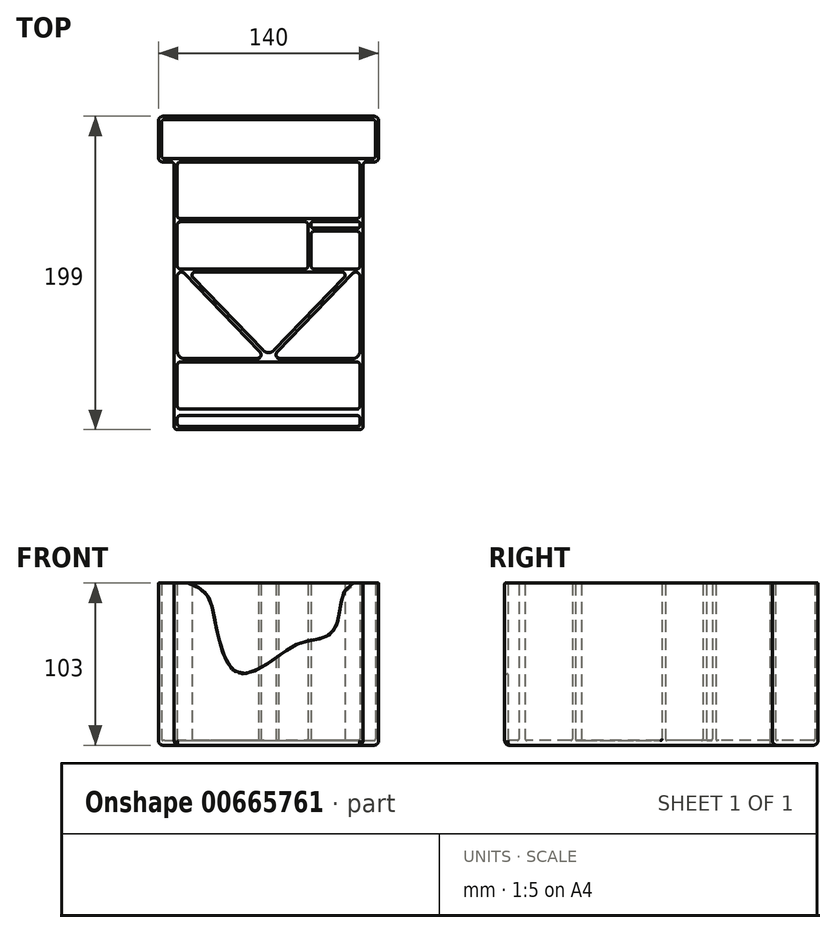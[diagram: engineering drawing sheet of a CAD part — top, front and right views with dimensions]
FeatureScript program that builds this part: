
annotation { "Feature Type Name" : "Feature", "Feature Type Description" : "" }
export const myFeature = defineFeature(function(context is Context, id is Id, definition is map)
    precondition{}
    {
        {
            var Q0;
            Q0=qCreatedBy(makeId("Top.planeOp"),FACE);
            var sketch = newSketch(context, id + "F0", { "sketchPlane" : qUnion([Q0])});
            skLineSegment(sketch, "E0.bottom", {"start": v(-61.93, 44.26) * mm, "end": v(-67, 44.26) * mm});
            skLineSegment(sketch, "E0.top", {"start": v(67, 73.26) * mm, "end": v(-67, 73.26) * mm});
            skLineSegment(sketch, "E0.left", {"start": v(70, 47.26) * mm, "end": v(70, 70.26) * mm});
            skLineSegment(sketch, "E0.right", {"start": v(-70, 47.26) * mm, "end": v(-70, 70.26) * mm});
            skPoint(sketch, "E0.middle", {"position": v(0, 58.76) * mm});
            skLineSegment(sketch, "E1", {"start": v(-70, 0) * mm, "end": v(70.86, 0) * mm, "construction": true});
            skLineSegment(sketch, "E2", {"start": v(-59.96, 42.57) * mm, "end": v(-59.96, -123.74) * mm});
            skLineSegment(sketch, "E3", {"start": v(60.04, 42.26) * mm, "end": v(60.04, -123.66) * mm});
            skLineSegment(sketch, "E4", {"start": v(57.04, 2.26) * mm, "end": v(28.04, 2.26) * mm});
            skLineSegment(sketch, "E5", {"start": v(-57.96, -125.74) * mm, "end": v(57.96, -125.74) * mm});
            skLineSegment(sketch, "E6.bottom", {"start": v(-55.96, 6.26) * mm, "end": v(23.04, 6.26) * mm});
            skLineSegment(sketch, "E6.top", {"start": v(-55.96, -23.74) * mm, "end": v(23.04, -23.74) * mm});
            skLineSegment(sketch, "E6.left", {"start": v(-57.96, 4.26) * mm, "end": v(-57.96, -21.74) * mm});
            skLineSegment(sketch, "E6.right", {"start": v(25.04, 4.26) * mm, "end": v(25.04, -21.74) * mm});
            skLineSegment(sketch, "E7.bottom", {"start": v(29.04, 0.26) * mm, "end": v(56.04, 0.26) * mm});
            skLineSegment(sketch, "E7.top", {"start": v(29.04, -23.74) * mm, "end": v(56.04, -23.74) * mm});
            skLineSegment(sketch, "E7.left", {"start": v(27.04, -1.74) * mm, "end": v(27.04, -21.74) * mm});
            skLineSegment(sketch, "E7.right", {"start": v(58.04, -1.74) * mm, "end": v(58.04, -21.74) * mm});
            skLineSegment(sketch, "E8", {"start": v(58.04, 3.26) * mm, "end": v(58.04, 5.26) * mm});
            skLineSegment(sketch, "E9", {"start": v(-46.62, -25.74) * mm, "end": v(46.62, -25.74) * mm});
            skLineSegment(sketch, "E10", {"start": v(-3.6, -75.32) * mm, "end": v(-48.06, -29.13) * mm});
            skPoint(sketch, "E11.newPointA", {"position": v(-10.52, -65.55) * mm});
            skPoint(sketch, "E12", {"position": v(0, -79.06) * mm});
            skPoint(sketch, "E13.visualSharp", {"position": v(-51.32, -25.74) * mm});
            skArc(sketch, "E13.filletArc", {"start": v(-46.62, -25.74) * mm, "mid": v(-48.46, -26.96) * mm, "end": v(-48.06, -29.13) * mm});
            skPoint(sketch, "E14.visualSharp", {"position": v(-57.96, -23.74) * mm});
            skArc(sketch, "E14.filletArc", {"start": v(-57.96, -21.74) * mm, "mid": v(-57.37, -23.16) * mm, "end": v(-55.96, -23.74) * mm});
            skPoint(sketch, "E15.visualSharp", {"position": v(25.04, -23.74) * mm});
            skArc(sketch, "E15.filletArc", {"start": v(23.04, -23.74) * mm, "mid": v(24.46, -23.16) * mm, "end": v(25.04, -21.74) * mm});
            skArc(sketch, "E16.filletArc", {"start": v(27.04, -21.74) * mm, "mid": v(27.63, -23.16) * mm, "end": v(29.04, -23.74) * mm});
            skPoint(sketch, "E17.visualSharp", {"position": v(25.04, 6.26) * mm});
            skArc(sketch, "E17.filletArc", {"start": v(25.04, 4.26) * mm, "mid": v(24.46, 5.67) * mm, "end": v(23.04, 6.26) * mm});
            skArc(sketch, "E18.filletArc", {"start": v(56.04, -23.74) * mm, "mid": v(57.46, -23.16) * mm, "end": v(58.04, -21.74) * mm});
            skPoint(sketch, "E19.visualSharp", {"position": v(-57.96, 6.26) * mm});
            skArc(sketch, "E19.filletArc", {"start": v(-55.96, 6.26) * mm, "mid": v(-57.37, 5.67) * mm, "end": v(-57.96, 4.26) * mm});
            skPoint(sketch, "E20.visualSharp", {"position": v(70, 44.26) * mm});
            skArc(sketch, "E20.filletArc", {"start": v(67, 44.26) * mm, "mid": v(69.12, 45.14) * mm, "end": v(70, 47.26) * mm});
            skPoint(sketch, "E21.visualSharp", {"position": v(-70, 44.26) * mm});
            skArc(sketch, "E21.filletArc", {"start": v(-70, 47.26) * mm, "mid": v(-69.12, 45.14) * mm, "end": v(-67, 44.26) * mm});
            skPoint(sketch, "E22.visualSharp", {"position": v(-70, 73.26) * mm});
            skArc(sketch, "E22.filletArc", {"start": v(-67, 73.26) * mm, "mid": v(-69.12, 72.38) * mm, "end": v(-70, 70.26) * mm});
            skPoint(sketch, "E23.visualSharp", {"position": v(70, 73.26) * mm});
            skArc(sketch, "E23.filletArc", {"start": v(70, 70.26) * mm, "mid": v(69.12, 72.38) * mm, "end": v(67, 73.26) * mm});
            skPoint(sketch, "E24.visualSharp", {"position": v(58, 1.67) * mm});
            skLineSegment(sketch, "E25", {"start": v(3.6, -75.32) * mm, "end": v(48.06, -29.13) * mm});
            skPoint(sketch, "E26.visualSharp", {"position": v(51.32, -25.74) * mm});
            skArc(sketch, "E26.filletArc", {"start": v(48.06, -29.13) * mm, "mid": v(48.46, -26.96) * mm, "end": v(46.62, -25.74) * mm});
            skArc(sketch, "E27.filletArc", {"start": v(-3.6, -75.32) * mm, "mid": v(0, -76.85) * mm, "end": v(3.6, -75.32) * mm});
            skPoint(sketch, "E28.startSnap0", {"position": v(0, -76.85) * mm});
            skArc(sketch, "E29.MirrorCS", {"start": v(53.28, -26.6) * mm, "mid": v(56.3, -25.94) * mm, "end": v(58.04, -28.51) * mm});
            skLineSegment(sketch, "E30.MirrorCS", {"start": v(58.04, -28.51) * mm, "end": v(58.04, -75.72) * mm});
            skArc(sketch, "E31.MirrorCS", {"start": v(58.04, -75.72) * mm, "mid": v(56.57, -79.28) * mm, "end": v(53, -80.76) * mm});
            skLineSegment(sketch, "E32.MirrorCS", {"start": v(5.61, -76.11) * mm, "end": v(53.28, -26.6) * mm});
            skLineSegment(sketch, "E33.MirrorCS", {"start": v(53, -80.76) * mm, "end": v(6.4, -80.76) * mm});
            skArc(sketch, "E34.MirrorCS", {"start": v(6.4, -80.76) * mm, "mid": v(4.83, -78.63) * mm, "end": v(5.61, -76.11) * mm});
            skLineSegment(sketch, "E35.bottom", {"start": v(-55.96, -82.76) * mm, "end": v(56.04, -82.76) * mm});
            skLineSegment(sketch, "E35.top", {"start": v(-55.96, -112.76) * mm, "end": v(56.04, -112.76) * mm});
            skLineSegment(sketch, "E35.left", {"start": v(-57.96, -84.76) * mm, "end": v(-57.96, -110.76) * mm});
            skLineSegment(sketch, "E35.right", {"start": v(58.04, -84.76) * mm, "end": v(58.04, -110.76) * mm});
            skPoint(sketch, "E36.visualSharp", {"position": v(-57.96, -82.76) * mm});
            skArc(sketch, "E36.filletArc", {"start": v(-55.96, -82.76) * mm, "mid": v(-57.37, -83.34) * mm, "end": v(-57.96, -84.76) * mm});
            skPoint(sketch, "E37.visualSharp", {"position": v(58.04, -82.76) * mm});
            skArc(sketch, "E37.filletArc", {"start": v(58.04, -84.76) * mm, "mid": v(57.46, -83.34) * mm, "end": v(56.04, -82.76) * mm});
            skPoint(sketch, "E38.visualSharp", {"position": v(58.04, -112.76) * mm});
            skArc(sketch, "E38.filletArc", {"start": v(56.04, -112.76) * mm, "mid": v(57.46, -112.17) * mm, "end": v(58.04, -110.76) * mm});
            skPoint(sketch, "E39.visualSharp", {"position": v(-57.96, -112.76) * mm});
            skArc(sketch, "E39.filletArc", {"start": v(-57.96, -110.76) * mm, "mid": v(-57.37, -112.17) * mm, "end": v(-55.96, -112.76) * mm});
            skLineSegment(sketch, "E40.bottom", {"start": v(-55.96, -116.74) * mm, "end": v(56.04, -116.74) * mm});
            skLineSegment(sketch, "E40.top", {"start": v(-55.96, -123.74) * mm, "end": v(56.04, -123.74) * mm});
            skLineSegment(sketch, "E40.left", {"start": v(-57.96, -118.74) * mm, "end": v(-57.96, -121.74) * mm});
            skLineSegment(sketch, "E40.right", {"start": v(58.04, -118.74) * mm, "end": v(58.04, -121.74) * mm});
            skPoint(sketch, "E41.visualSharp", {"position": v(58.04, -116.74) * mm});
            skArc(sketch, "E41.filletArc", {"start": v(58.04, -118.74) * mm, "mid": v(57.46, -117.33) * mm, "end": v(56.04, -116.74) * mm});
            skPoint(sketch, "E42.visualSharp", {"position": v(58.04, -123.74) * mm});
            skArc(sketch, "E42.filletArc", {"start": v(56.04, -123.74) * mm, "mid": v(57.46, -123.16) * mm, "end": v(58.04, -121.74) * mm});
            skPoint(sketch, "E43.visualSharp", {"position": v(-57.96, -123.74) * mm});
            skArc(sketch, "E43.filletArc", {"start": v(-57.96, -121.74) * mm, "mid": v(-57.37, -123.16) * mm, "end": v(-55.96, -123.74) * mm});
            skPoint(sketch, "E44.visualSharp", {"position": v(-57.96, -116.74) * mm});
            skArc(sketch, "E44.filletArc", {"start": v(-55.96, -116.74) * mm, "mid": v(-57.37, -117.33) * mm, "end": v(-57.96, -118.74) * mm});
            skLineSegment(sketch, "E45.bottom", {"start": v(-66, 71.26) * mm, "end": v(66, 71.26) * mm});
            skLineSegment(sketch, "E45.top", {"start": v(-66, 46.26) * mm, "end": v(66, 46.26) * mm});
            skLineSegment(sketch, "E45.left", {"start": v(-68, 69.26) * mm, "end": v(-68, 48.26) * mm});
            skLineSegment(sketch, "E45.right", {"start": v(68, 69.26) * mm, "end": v(68, 48.26) * mm});
            skPoint(sketch, "E46.visualSharp", {"position": v(-68, 71.26) * mm});
            skArc(sketch, "E46.filletArc", {"start": v(-66, 71.26) * mm, "mid": v(-67.41, 70.67) * mm, "end": v(-68, 69.26) * mm});
            skPoint(sketch, "E47.visualSharp", {"position": v(-68, 46.26) * mm});
            skArc(sketch, "E47.filletArc", {"start": v(-68, 48.26) * mm, "mid": v(-67.41, 46.84) * mm, "end": v(-66, 46.26) * mm});
            skPoint(sketch, "E48.visualSharp", {"position": v(68, 46.26) * mm});
            skArc(sketch, "E48.filletArc", {"start": v(66, 46.26) * mm, "mid": v(67.41, 46.84) * mm, "end": v(68, 48.26) * mm});
            skPoint(sketch, "E49.visualSharp", {"position": v(68, 71.26) * mm});
            skArc(sketch, "E49.filletArc", {"start": v(68, 69.26) * mm, "mid": v(67.41, 70.67) * mm, "end": v(66, 71.26) * mm});
            skLineSegment(sketch, "E50.bottom", {"start": v(-56, 44.26) * mm, "end": v(56, 44.26) * mm});
            skLineSegment(sketch, "E50.top", {"start": v(-56, 8.26) * mm, "end": v(56, 8.26) * mm});
            skLineSegment(sketch, "E50.left", {"start": v(-58, 42.26) * mm, "end": v(-58, 10.26) * mm});
            skLineSegment(sketch, "E50.right", {"start": v(58, 42.26) * mm, "end": v(58, 10.26) * mm});
            skPoint(sketch, "E51.newPointA", {"position": v(-60, 44.74) * mm});
            skArc(sketch, "E51.filletArc", {"start": v(-59.94, 42.4) * mm, "mid": v(-60.57, 43.72) * mm, "end": v(-61.93, 44.26) * mm});
            skPoint(sketch, "E52.visualSharp", {"position": v(-58, 44.26) * mm});
            skArc(sketch, "E52.filletArc", {"start": v(-56, 44.26) * mm, "mid": v(-57.41, 43.67) * mm, "end": v(-58, 42.26) * mm});
            skPoint(sketch, "E53.visualSharp", {"position": v(58, 44.26) * mm});
            skArc(sketch, "E53.filletArc", {"start": v(58, 42.26) * mm, "mid": v(57.41, 43.67) * mm, "end": v(56, 44.26) * mm});
            skPoint(sketch, "E54.visualSharp", {"position": v(58, 8.26) * mm});
            skArc(sketch, "E54.filletArc", {"start": v(56, 8.26) * mm, "mid": v(57.41, 8.84) * mm, "end": v(58, 10.26) * mm});
            skPoint(sketch, "E55.visualSharp", {"position": v(-58, 8.26) * mm});
            skArc(sketch, "E55.filletArc", {"start": v(-58, 10.26) * mm, "mid": v(-57.41, 8.84) * mm, "end": v(-56, 8.26) * mm});
            skLineSegment(sketch, "E56", {"start": v(67, 44.26) * mm, "end": v(62.04, 44.26) * mm});
            skPoint(sketch, "E57.visualSharp", {"position": v(60, 44.26) * mm});
            skArc(sketch, "E57.filletArc", {"start": v(62.04, 44.26) * mm, "mid": v(60.63, 43.67) * mm, "end": v(60.04, 42.26) * mm});
            skLineSegment(sketch, "E58", {"start": v(57.04, 6.26) * mm, "end": v(28.04, 6.26) * mm});
            skLineSegment(sketch, "E59", {"start": v(27.04, 5.26) * mm, "end": v(27.04, 3.26) * mm});
            skArc(sketch, "E60.filletArc", {"start": v(58.04, 5.26) * mm, "mid": v(57.75, 5.96) * mm, "end": v(57.04, 6.26) * mm});
            skPoint(sketch, "E61.visualSharp", {"position": v(58.04, 2.26) * mm});
            skArc(sketch, "E61.filletArc", {"start": v(57.04, 2.26) * mm, "mid": v(57.75, 2.55) * mm, "end": v(58.04, 3.26) * mm});
            skPoint(sketch, "E62.visualSharp", {"position": v(27.04, 6.26) * mm});
            skArc(sketch, "E62.filletArc", {"start": v(28.04, 6.26) * mm, "mid": v(27.34, 5.96) * mm, "end": v(27.04, 5.26) * mm});
            skPoint(sketch, "E63.visualSharp", {"position": v(27.04, 2.26) * mm});
            skArc(sketch, "E63.filletArc", {"start": v(27.04, 3.26) * mm, "mid": v(27.34, 2.55) * mm, "end": v(28.04, 2.26) * mm});
            skPoint(sketch, "E64.visualSharp", {"position": v(27.04, 0.26) * mm});
            skArc(sketch, "E64.filletArc", {"start": v(29.04, 0.26) * mm, "mid": v(27.63, -0.33) * mm, "end": v(27.04, -1.74) * mm});
            skPoint(sketch, "E65.visualSharp", {"position": v(58.04, 0.26) * mm});
            skArc(sketch, "E65.filletArc", {"start": v(58.04, -1.74) * mm, "mid": v(57.46, -0.33) * mm, "end": v(56.04, 0.26) * mm});
            skPoint(sketch, "E66.orphan", {"position": v(-59.96, 9.74) * mm});
            skPoint(sketch, "E67.visualSharp", {"position": v(60.04, -125.74) * mm});
            skArc(sketch, "E67.filletArc", {"start": v(57.96, -125.74) * mm, "mid": v(59.43, -125.13) * mm, "end": v(60.04, -123.66) * mm});
            skLineSegment(sketch, "E68", {"start": v(-62.4, -25.74) * mm, "end": v(73.57, -25.74) * mm, "construction": true});
            skLineSegment(sketch, "E69", {"start": v(0, 0) * mm, "end": v(0, -125.74) * mm, "construction": true});
            skArc(sketch, "E70.MirrorCS", {"start": v(-58.04, -75.72) * mm, "mid": v(-56.57, -79.28) * mm, "end": v(-53, -80.76) * mm});
            skLineSegment(sketch, "E71.MirrorCS", {"start": v(-53, -80.76) * mm, "end": v(-6.4, -80.76) * mm});
            skArc(sketch, "E72.MirrorCS", {"start": v(-6.4, -80.76) * mm, "mid": v(-4.83, -78.63) * mm, "end": v(-5.61, -76.11) * mm});
            skLineSegment(sketch, "E73.MirrorCS", {"start": v(-58.04, -28.51) * mm, "end": v(-58.04, -75.72) * mm});
            skLineSegment(sketch, "E74.MirrorCS", {"start": v(-5.61, -76.11) * mm, "end": v(-53.28, -26.6) * mm});
            skArc(sketch, "E75.MirrorCS", {"start": v(-53.28, -26.6) * mm, "mid": v(-56.3, -25.94) * mm, "end": v(-58.04, -28.51) * mm});
            skPoint(sketch, "E76.orphan", {"position": v(-57.96, -125.74) * mm});
            skArc(sketch, "E77.filletArc", {"start": v(-59.96, -123.74) * mm, "mid": v(-59.37, -125.16) * mm, "end": v(-57.96, -125.74) * mm});
            skSolve(sketch);
        }
        {
            var Q0;
            {var subQ2=sQuery(id+"F0.wireOp",EDGE,"E0.bottom");Q0=makeQuery(id+"F0.imprint","IMPRINT",FACE,{"disambiguationData":[TD([[makeQuery(id+"F0.imprint","IMPRINT",EDGE,{"derivedFrom":subQ2}),-1.0]])]});}
            extrude(context, id + "F1", {"entities" : qUnion([Q0]), "depth" : 100 * mm, "offsetDistance" : 25 * mm});
        }
        {
            var Q0;
            Q0=makeQuery(id+"F1.opExtrude","SWEPT_FACE",FACE,{"disambiguationData":[OSD([sQuery(id+"F0.wireOp",EDGE,"E5")])]});
            var sketch = newSketch(context, id + "F2", { "sketchPlane" : qUnion([Q0])});
            skFitSpline(sketch, "E78", {"points": [v(-51.01, 100) * mm, v(-41.25, 94.71) * mm, v(-35.92, 85.04) * mm, v(-20.77, 43.42) * mm, v(7.8, 54.88) * mm, v(23.55, 62.94) * mm, v(39.5, 67.79) * mm, v(45.73, 85.04) * mm, v(54.22, 100) * mm], "startDerivative": vector(104.02, -12.85) * mm, "endDerivative": vector(161.57, 51.13) * mm});
            skLineSegment(sketch, "E79", {"start": v(-51.01, 100) * mm, "end": v(54.22, 100) * mm});
            skSolve(sketch);
        }
        {
            var Q0;
            Q0 = qSketchRegion(id + "F2", true);
            extrude(context, id + "F3", {"entities" : qUnion([Q0]), "operationType" : NewBodyOperationType.REMOVE, "oppositeDirection" : true, "depth" : 3 * mm, "offsetDistance" : 25 * mm});
        }
        {
            var Q0;
            Q0=qCreatedBy(makeId("Top.planeOp"),FACE);
            var sketch = newSketch(context, id + "F4", { "sketchPlane" : qUnion([Q0])});
            skLineSegment(sketch, "E80.0", {"start": v(-59.96, 42.57) * mm, "end": v(-59.96, -123.74) * mm});
            skLineSegment(sketch, "E80.2", {"start": v(-57.96, -125.74) * mm, "end": v(57.96, -125.74) * mm});
            skArc(sketch, "E80.3", {"start": v(57.96, -125.74) * mm, "mid": v(59.43, -125.13) * mm, "end": v(60.04, -123.66) * mm});
            skLineSegment(sketch, "E80.4", {"start": v(60.04, 42.26) * mm, "end": v(60.04, -123.66) * mm});
            skArc(sketch, "E80.5", {"start": v(-59.94, 42.4) * mm, "mid": v(-60.57, 43.72) * mm, "end": v(-61.93, 44.26) * mm});
            skLineSegment(sketch, "E80.6", {"start": v(-61.93, 44.26) * mm, "end": v(-67, 44.26) * mm});
            skArc(sketch, "E80.7", {"start": v(-70, 47.26) * mm, "mid": v(-69.12, 45.14) * mm, "end": v(-67, 44.26) * mm});
            skLineSegment(sketch, "E80.8", {"start": v(-70, 47.26) * mm, "end": v(-70, 70.26) * mm});
            skArc(sketch, "E80.9", {"start": v(-67, 73.26) * mm, "mid": v(-69.12, 72.38) * mm, "end": v(-70, 70.26) * mm});
            skLineSegment(sketch, "E80.10", {"start": v(67, 73.26) * mm, "end": v(-67, 73.26) * mm});
            skArc(sketch, "E80.11", {"start": v(70, 70.26) * mm, "mid": v(69.12, 72.38) * mm, "end": v(67, 73.26) * mm});
            skLineSegment(sketch, "E80.12", {"start": v(70, 47.26) * mm, "end": v(70, 70.26) * mm});
            skArc(sketch, "E80.13", {"start": v(67, 44.26) * mm, "mid": v(69.12, 45.14) * mm, "end": v(70, 47.26) * mm});
            skLineSegment(sketch, "E80.14", {"start": v(67, 44.26) * mm, "end": v(62.04, 44.26) * mm});
            skArc(sketch, "E80.15", {"start": v(62.04, 44.26) * mm, "mid": v(60.63, 43.67) * mm, "end": v(60.04, 42.26) * mm});
            skPoint(sketch, "E80.16", {"position": v(60.63, 43.67) * mm});
            skArc(sketch, "E81.0", {"start": v(-59.96, -123.74) * mm, "mid": v(-59.37, -125.16) * mm, "end": v(-57.96, -125.74) * mm});
            skSolve(sketch);
        }
        {
            var Q0;
            Q0 = qSketchRegion(id + "F4", true);
            extrude(context, id + "F5", {"entities" : qUnion([Q0]), "operationType" : NewBodyOperationType.ADD, "oppositeDirection" : true, "depth" : 3 * mm, "offsetDistance" : 25 * mm});
        }
        {
            var Q0;
            Q0=makeQuery(id+"F5.opExtrude","CAP_EDGE",EDGE,{"disambiguationData":[OSD([sQuery(id+"F4.wireOp",EDGE,"E80.2")])],"isStart":false});
            fillet(context, id + "F6", {"entities" : qUnion([Q0]), "radius" : 3 * mm, "tangentPropagation" : true, "allowEdgeOverflow" : false});
        }
        {
            var Q0;
            Q0=makeQuery(id+"F3.boolean.opBoolean","COPY",EDGE,{"derivedFrom":makeQuery(id+"F3.opExtrude","CAP_EDGE",EDGE,{"disambiguationData":[OSD([sQuery(id+"F2.wireOp",EDGE,"E78")])],"isStart":true})});
            var Q1;
            {var subQ0=sQuery(id+"F0.wireOp",EDGE,"E77.filletArc");var subQ1=sQuery(id+"F0.wireOp",EDGE,"E5");Q1=makeQuery(id+"F3.boolean.opBoolean","SPLIT",EDGE,{"disambiguationData":[TD([makeQuery(id+"F1.opExtrude","SWEPT_FACE",FACE,{"disambiguationData":[OSD([subQ0])]})])],"derivedFrom":makeQuery(id+"F1.opExtrude","CAP_EDGE",EDGE,{"disambiguationData":[OSD([subQ1])],"isStart":false})});}
            var Q2;
            {var subQ0=sQuery(id+"F0.wireOp",EDGE,"E67.filletArc");var subQ1=sQuery(id+"F0.wireOp",EDGE,"E5");Q2=makeQuery(id+"F3.boolean.opBoolean","SPLIT",EDGE,{"disambiguationData":[TD([makeQuery(id+"F1.opExtrude","SWEPT_FACE",FACE,{"disambiguationData":[OSD([subQ0])]})])],"derivedFrom":makeQuery(id+"F1.opExtrude","CAP_EDGE",EDGE,{"disambiguationData":[OSD([subQ1])],"isStart":false})});}
            var Q3;
            {var subQ0=sQuery(id+"F0.wireOp",EDGE,"E42.filletArc");var subQ1=sQuery(id+"F0.wireOp",EDGE,"E40.top");Q3=makeQuery(id+"F3.boolean.opBoolean","SPLIT",EDGE,{"disambiguationData":[TD([makeQuery(id+"F1.opExtrude","SWEPT_FACE",FACE,{"disambiguationData":[OSD([subQ0])]})])],"derivedFrom":makeQuery(id+"F1.opExtrude","CAP_EDGE",EDGE,{"disambiguationData":[OSD([subQ1])],"isStart":false})});}
            var Q4;
            Q4=makeQuery(id+"F3.boolean.opBoolean","INTERSECT",EDGE,{"derivedFrom":[makeQuery(id+"F1.opExtrude","SWEPT_FACE",FACE,{"disambiguationData":[OSD([sQuery(id+"F0.wireOp",EDGE,"E40.top")])]}),makeQuery(id+"F3.opExtrude","SWEPT_FACE",FACE,{"disambiguationData":[OSD([sQuery(id+"F2.wireOp",EDGE,"E78")])]})]});
            fillet(context, id + "F7", {"entities" : qUnion([Q0, Q1, Q2, Q3, Q4]), "radius" : 0.5 * mm, "tangentPropagation" : true, "allowEdgeOverflow" : false});
        }
        {
            var Q0;
            Q0=makeQuery(id+"F1.opExtrude","CAP_EDGE",EDGE,{"disambiguationData":[OSD([sQuery(id+"F0.wireOp",EDGE,"E45.bottom")])],"isStart":false});
            var Q1;
            Q1=makeQuery(id+"F1.opExtrude","CAP_EDGE",EDGE,{"disambiguationData":[OSD([sQuery(id+"F0.wireOp",EDGE,"E50.bottom")])],"isStart":false});
            var Q2;
            Q2=makeQuery(id+"F1.opExtrude","CAP_EDGE",EDGE,{"disambiguationData":[OSD([sQuery(id+"F0.wireOp",EDGE,"E58")])],"isStart":false});
            var Q3;
            Q3=makeQuery(id+"F1.opExtrude","CAP_EDGE",EDGE,{"disambiguationData":[OSD([sQuery(id+"F0.wireOp",EDGE,"E6.bottom")])],"isStart":false});
            var Q4;
            Q4=makeQuery(id+"F1.opExtrude","CAP_EDGE",EDGE,{"disambiguationData":[OSD([sQuery(id+"F0.wireOp",EDGE,"E7.bottom")])],"isStart":false});
            var Q5;
            Q5=makeQuery(id+"F1.opExtrude","CAP_EDGE",EDGE,{"disambiguationData":[OSD([sQuery(id+"F0.wireOp",EDGE,"E9")])],"isStart":false});
            var Q6;
            Q6=makeQuery(id+"F1.opExtrude","CAP_EDGE",EDGE,{"disambiguationData":[OSD([sQuery(id+"F0.wireOp",EDGE,"E29.MirrorCS")])],"isStart":false});
            var Q7;
            Q7=makeQuery(id+"F1.opExtrude","CAP_EDGE",EDGE,{"disambiguationData":[OSD([sQuery(id+"F0.wireOp",EDGE,"E74.MirrorCS")])],"isStart":false});
            var Q8;
            Q8=makeQuery(id+"F1.opExtrude","CAP_EDGE",EDGE,{"disambiguationData":[OSD([sQuery(id+"F0.wireOp",EDGE,"E35.bottom")])],"isStart":false});
            fillet(context, id + "F8", {"entities" : qUnion([Q0, Q1, Q2, Q3, Q4, Q5, Q6, Q7, Q8]), "radius" : 0.5 * mm, "tangentPropagation" : true, "allowEdgeOverflow" : false});
        }
        {
            var Q0;
            Q0=makeQuery(id+"F5.boolean.opBoolean","SPLIT",FACE,{"disambiguationData":[TD([makeQuery(id+"F1.opExtrude","SWEPT_FACE",FACE,{"disambiguationData":[OSD([sQuery(id+"F0.wireOp",EDGE,"E45.bottom")])]})])],"derivedFrom":makeQuery(id+"F5.opExtrude","CAP_FACE",FACE,{"disambiguationData":[OSD([sQuery(id+"F4.wireOp",EDGE,"E80.0"),sQuery(id+"F4.wireOp",EDGE,"E80.2"),sQuery(id+"F4.wireOp",EDGE,"E80.3"),sQuery(id+"F4.wireOp",EDGE,"E80.4"),sQuery(id+"F4.wireOp",EDGE,"E80.5"),sQuery(id+"F4.wireOp",EDGE,"E80.6"),sQuery(id+"F4.wireOp",EDGE,"E80.7"),sQuery(id+"F4.wireOp",EDGE,"E80.8"),sQuery(id+"F4.wireOp",EDGE,"E80.9"),sQuery(id+"F4.wireOp",EDGE,"E80.10"),sQuery(id+"F4.wireOp",EDGE,"E80.11"),sQuery(id+"F4.wireOp",EDGE,"E80.12"),sQuery(id+"F4.wireOp",EDGE,"E80.13"),sQuery(id+"F4.wireOp",EDGE,"E80.14"),sQuery(id+"F4.wireOp",EDGE,"E80.15"),sQuery(id+"F4.wireOp",EDGE,"E81.0")])],"isStart":true})});
            var Q1;
            Q1=makeQuery(id+"F5.boolean.opBoolean","SPLIT",FACE,{"disambiguationData":[TD([makeQuery(id+"F1.opExtrude","SWEPT_FACE",FACE,{"disambiguationData":[OSD([sQuery(id+"F0.wireOp",EDGE,"E50.bottom")])]})])],"derivedFrom":makeQuery(id+"F5.opExtrude","CAP_FACE",FACE,{"disambiguationData":[OSD([sQuery(id+"F4.wireOp",EDGE,"E80.0"),sQuery(id+"F4.wireOp",EDGE,"E80.2"),sQuery(id+"F4.wireOp",EDGE,"E80.3"),sQuery(id+"F4.wireOp",EDGE,"E80.4"),sQuery(id+"F4.wireOp",EDGE,"E80.5"),sQuery(id+"F4.wireOp",EDGE,"E80.6"),sQuery(id+"F4.wireOp",EDGE,"E80.7"),sQuery(id+"F4.wireOp",EDGE,"E80.8"),sQuery(id+"F4.wireOp",EDGE,"E80.9"),sQuery(id+"F4.wireOp",EDGE,"E80.10"),sQuery(id+"F4.wireOp",EDGE,"E80.11"),sQuery(id+"F4.wireOp",EDGE,"E80.12"),sQuery(id+"F4.wireOp",EDGE,"E80.13"),sQuery(id+"F4.wireOp",EDGE,"E80.14"),sQuery(id+"F4.wireOp",EDGE,"E80.15"),sQuery(id+"F4.wireOp",EDGE,"E81.0")])],"isStart":true})});
            var Q2;
            Q2=makeQuery(id+"F5.boolean.opBoolean","SPLIT",FACE,{"disambiguationData":[TD([makeQuery(id+"F1.opExtrude","SWEPT_FACE",FACE,{"disambiguationData":[OSD([sQuery(id+"F0.wireOp",EDGE,"E6.bottom")])]})])],"derivedFrom":makeQuery(id+"F5.opExtrude","CAP_FACE",FACE,{"disambiguationData":[OSD([sQuery(id+"F4.wireOp",EDGE,"E80.0"),sQuery(id+"F4.wireOp",EDGE,"E80.2"),sQuery(id+"F4.wireOp",EDGE,"E80.3"),sQuery(id+"F4.wireOp",EDGE,"E80.4"),sQuery(id+"F4.wireOp",EDGE,"E80.5"),sQuery(id+"F4.wireOp",EDGE,"E80.6"),sQuery(id+"F4.wireOp",EDGE,"E80.7"),sQuery(id+"F4.wireOp",EDGE,"E80.8"),sQuery(id+"F4.wireOp",EDGE,"E80.9"),sQuery(id+"F4.wireOp",EDGE,"E80.10"),sQuery(id+"F4.wireOp",EDGE,"E80.11"),sQuery(id+"F4.wireOp",EDGE,"E80.12"),sQuery(id+"F4.wireOp",EDGE,"E80.13"),sQuery(id+"F4.wireOp",EDGE,"E80.14"),sQuery(id+"F4.wireOp",EDGE,"E80.15"),sQuery(id+"F4.wireOp",EDGE,"E81.0")])],"isStart":true})});
            var Q3;
            Q3=makeQuery(id+"F5.boolean.opBoolean","SPLIT",FACE,{"disambiguationData":[TD([makeQuery(id+"F1.opExtrude","SWEPT_FACE",FACE,{"disambiguationData":[OSD([sQuery(id+"F0.wireOp",EDGE,"E4")])]})])],"derivedFrom":makeQuery(id+"F5.opExtrude","CAP_FACE",FACE,{"disambiguationData":[OSD([sQuery(id+"F4.wireOp",EDGE,"E80.0"),sQuery(id+"F4.wireOp",EDGE,"E80.2"),sQuery(id+"F4.wireOp",EDGE,"E80.3"),sQuery(id+"F4.wireOp",EDGE,"E80.4"),sQuery(id+"F4.wireOp",EDGE,"E80.5"),sQuery(id+"F4.wireOp",EDGE,"E80.6"),sQuery(id+"F4.wireOp",EDGE,"E80.7"),sQuery(id+"F4.wireOp",EDGE,"E80.8"),sQuery(id+"F4.wireOp",EDGE,"E80.9"),sQuery(id+"F4.wireOp",EDGE,"E80.10"),sQuery(id+"F4.wireOp",EDGE,"E80.11"),sQuery(id+"F4.wireOp",EDGE,"E80.12"),sQuery(id+"F4.wireOp",EDGE,"E80.13"),sQuery(id+"F4.wireOp",EDGE,"E80.14"),sQuery(id+"F4.wireOp",EDGE,"E80.15"),sQuery(id+"F4.wireOp",EDGE,"E81.0")])],"isStart":true})});
            var Q4;
            Q4=makeQuery(id+"F5.boolean.opBoolean","SPLIT",FACE,{"disambiguationData":[TD([makeQuery(id+"F1.opExtrude","SWEPT_FACE",FACE,{"disambiguationData":[OSD([sQuery(id+"F0.wireOp",EDGE,"E7.bottom")])]})])],"derivedFrom":makeQuery(id+"F5.opExtrude","CAP_FACE",FACE,{"disambiguationData":[OSD([sQuery(id+"F4.wireOp",EDGE,"E80.0"),sQuery(id+"F4.wireOp",EDGE,"E80.2"),sQuery(id+"F4.wireOp",EDGE,"E80.3"),sQuery(id+"F4.wireOp",EDGE,"E80.4"),sQuery(id+"F4.wireOp",EDGE,"E80.5"),sQuery(id+"F4.wireOp",EDGE,"E80.6"),sQuery(id+"F4.wireOp",EDGE,"E80.7"),sQuery(id+"F4.wireOp",EDGE,"E80.8"),sQuery(id+"F4.wireOp",EDGE,"E80.9"),sQuery(id+"F4.wireOp",EDGE,"E80.10"),sQuery(id+"F4.wireOp",EDGE,"E80.11"),sQuery(id+"F4.wireOp",EDGE,"E80.12"),sQuery(id+"F4.wireOp",EDGE,"E80.13"),sQuery(id+"F4.wireOp",EDGE,"E80.14"),sQuery(id+"F4.wireOp",EDGE,"E80.15"),sQuery(id+"F4.wireOp",EDGE,"E81.0")])],"isStart":true})});
            var Q5;
            Q5=makeQuery(id+"F5.boolean.opBoolean","SPLIT",FACE,{"disambiguationData":[TD([makeQuery(id+"F1.opExtrude","SWEPT_FACE",FACE,{"disambiguationData":[OSD([sQuery(id+"F0.wireOp",EDGE,"E9")])]})])],"derivedFrom":makeQuery(id+"F5.opExtrude","CAP_FACE",FACE,{"disambiguationData":[OSD([sQuery(id+"F4.wireOp",EDGE,"E80.0"),sQuery(id+"F4.wireOp",EDGE,"E80.2"),sQuery(id+"F4.wireOp",EDGE,"E80.3"),sQuery(id+"F4.wireOp",EDGE,"E80.4"),sQuery(id+"F4.wireOp",EDGE,"E80.5"),sQuery(id+"F4.wireOp",EDGE,"E80.6"),sQuery(id+"F4.wireOp",EDGE,"E80.7"),sQuery(id+"F4.wireOp",EDGE,"E80.8"),sQuery(id+"F4.wireOp",EDGE,"E80.9"),sQuery(id+"F4.wireOp",EDGE,"E80.10"),sQuery(id+"F4.wireOp",EDGE,"E80.11"),sQuery(id+"F4.wireOp",EDGE,"E80.12"),sQuery(id+"F4.wireOp",EDGE,"E80.13"),sQuery(id+"F4.wireOp",EDGE,"E80.14"),sQuery(id+"F4.wireOp",EDGE,"E80.15"),sQuery(id+"F4.wireOp",EDGE,"E81.0")])],"isStart":true})});
            var Q6;
            Q6=makeQuery(id+"F5.boolean.opBoolean","SPLIT",FACE,{"disambiguationData":[TD([makeQuery(id+"F1.opExtrude","SWEPT_FACE",FACE,{"disambiguationData":[OSD([sQuery(id+"F0.wireOp",EDGE,"E29.MirrorCS")])]})])],"derivedFrom":makeQuery(id+"F5.opExtrude","CAP_FACE",FACE,{"disambiguationData":[OSD([sQuery(id+"F4.wireOp",EDGE,"E80.0"),sQuery(id+"F4.wireOp",EDGE,"E80.2"),sQuery(id+"F4.wireOp",EDGE,"E80.3"),sQuery(id+"F4.wireOp",EDGE,"E80.4"),sQuery(id+"F4.wireOp",EDGE,"E80.5"),sQuery(id+"F4.wireOp",EDGE,"E80.6"),sQuery(id+"F4.wireOp",EDGE,"E80.7"),sQuery(id+"F4.wireOp",EDGE,"E80.8"),sQuery(id+"F4.wireOp",EDGE,"E80.9"),sQuery(id+"F4.wireOp",EDGE,"E80.10"),sQuery(id+"F4.wireOp",EDGE,"E80.11"),sQuery(id+"F4.wireOp",EDGE,"E80.12"),sQuery(id+"F4.wireOp",EDGE,"E80.13"),sQuery(id+"F4.wireOp",EDGE,"E80.14"),sQuery(id+"F4.wireOp",EDGE,"E80.15"),sQuery(id+"F4.wireOp",EDGE,"E81.0")])],"isStart":true})});
            var Q7;
            Q7=makeQuery(id+"F5.boolean.opBoolean","SPLIT",FACE,{"disambiguationData":[TD([makeQuery(id+"F1.opExtrude","SWEPT_FACE",FACE,{"disambiguationData":[OSD([sQuery(id+"F0.wireOp",EDGE,"E70.MirrorCS")])]})])],"derivedFrom":makeQuery(id+"F5.opExtrude","CAP_FACE",FACE,{"disambiguationData":[OSD([sQuery(id+"F4.wireOp",EDGE,"E80.0"),sQuery(id+"F4.wireOp",EDGE,"E80.2"),sQuery(id+"F4.wireOp",EDGE,"E80.3"),sQuery(id+"F4.wireOp",EDGE,"E80.4"),sQuery(id+"F4.wireOp",EDGE,"E80.5"),sQuery(id+"F4.wireOp",EDGE,"E80.6"),sQuery(id+"F4.wireOp",EDGE,"E80.7"),sQuery(id+"F4.wireOp",EDGE,"E80.8"),sQuery(id+"F4.wireOp",EDGE,"E80.9"),sQuery(id+"F4.wireOp",EDGE,"E80.10"),sQuery(id+"F4.wireOp",EDGE,"E80.11"),sQuery(id+"F4.wireOp",EDGE,"E80.12"),sQuery(id+"F4.wireOp",EDGE,"E80.13"),sQuery(id+"F4.wireOp",EDGE,"E80.14"),sQuery(id+"F4.wireOp",EDGE,"E80.15"),sQuery(id+"F4.wireOp",EDGE,"E81.0")])],"isStart":true})});
            var Q8;
            Q8=makeQuery(id+"F5.boolean.opBoolean","SPLIT",FACE,{"disambiguationData":[TD([makeQuery(id+"F1.opExtrude","SWEPT_FACE",FACE,{"disambiguationData":[OSD([sQuery(id+"F0.wireOp",EDGE,"E35.bottom")])]})])],"derivedFrom":makeQuery(id+"F5.opExtrude","CAP_FACE",FACE,{"disambiguationData":[OSD([sQuery(id+"F4.wireOp",EDGE,"E80.0"),sQuery(id+"F4.wireOp",EDGE,"E80.2"),sQuery(id+"F4.wireOp",EDGE,"E80.3"),sQuery(id+"F4.wireOp",EDGE,"E80.4"),sQuery(id+"F4.wireOp",EDGE,"E80.5"),sQuery(id+"F4.wireOp",EDGE,"E80.6"),sQuery(id+"F4.wireOp",EDGE,"E80.7"),sQuery(id+"F4.wireOp",EDGE,"E80.8"),sQuery(id+"F4.wireOp",EDGE,"E80.9"),sQuery(id+"F4.wireOp",EDGE,"E80.10"),sQuery(id+"F4.wireOp",EDGE,"E80.11"),sQuery(id+"F4.wireOp",EDGE,"E80.12"),sQuery(id+"F4.wireOp",EDGE,"E80.13"),sQuery(id+"F4.wireOp",EDGE,"E80.14"),sQuery(id+"F4.wireOp",EDGE,"E80.15"),sQuery(id+"F4.wireOp",EDGE,"E81.0")])],"isStart":true})});
            var Q9;
            Q9=makeQuery(id+"F5.boolean.opBoolean","SPLIT",FACE,{"disambiguationData":[TD([makeQuery(id+"F1.opExtrude","SWEPT_FACE",FACE,{"disambiguationData":[OSD([sQuery(id+"F0.wireOp",EDGE,"E40.bottom")])]})])],"derivedFrom":makeQuery(id+"F5.opExtrude","CAP_FACE",FACE,{"disambiguationData":[OSD([sQuery(id+"F4.wireOp",EDGE,"E80.0"),sQuery(id+"F4.wireOp",EDGE,"E80.2"),sQuery(id+"F4.wireOp",EDGE,"E80.3"),sQuery(id+"F4.wireOp",EDGE,"E80.4"),sQuery(id+"F4.wireOp",EDGE,"E80.5"),sQuery(id+"F4.wireOp",EDGE,"E80.6"),sQuery(id+"F4.wireOp",EDGE,"E80.7"),sQuery(id+"F4.wireOp",EDGE,"E80.8"),sQuery(id+"F4.wireOp",EDGE,"E80.9"),sQuery(id+"F4.wireOp",EDGE,"E80.10"),sQuery(id+"F4.wireOp",EDGE,"E80.11"),sQuery(id+"F4.wireOp",EDGE,"E80.12"),sQuery(id+"F4.wireOp",EDGE,"E80.13"),sQuery(id+"F4.wireOp",EDGE,"E80.14"),sQuery(id+"F4.wireOp",EDGE,"E80.15"),sQuery(id+"F4.wireOp",EDGE,"E81.0")])],"isStart":true})});
            fillet(context, id + "F9", {"entities" : qUnion([Q0, Q1, Q2, Q3, Q4, Q5, Q6, Q7, Q8, Q9]), "radius" : 1 * mm, "tangentPropagation" : true, "allowEdgeOverflow" : false});
        }
    });
